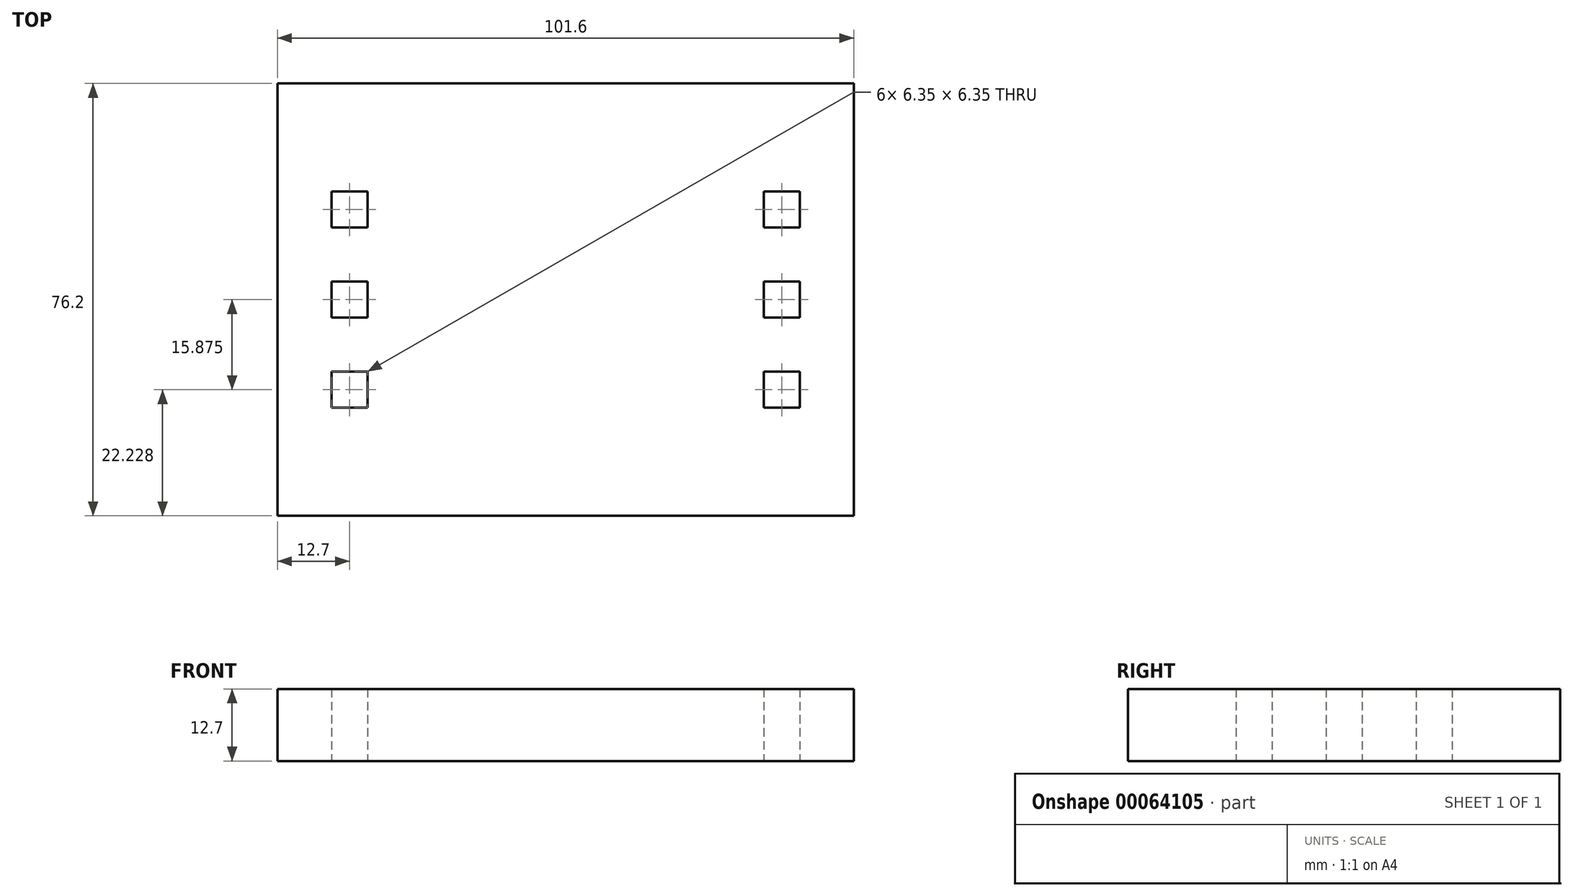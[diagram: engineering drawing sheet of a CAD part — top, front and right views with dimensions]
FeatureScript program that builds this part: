
annotation { "Feature Type Name" : "Feature", "Feature Type Description" : "" }
export const myFeature = defineFeature(function(context is Context, id is Id, definition is map)
    precondition{}
    {
        {
            var Q0;
            Q0=qCreatedBy(makeId("Top.planeOp"),FACE);
            var sketch = newSketch(context, id + "F0", { "sketchPlane" : qUnion([Q0])});
            skLineSegment(sketch, "E0.bottom", {"start": v(-40.85, 46.24) * mm, "end": v(60.75, 46.24) * mm});
            skLineSegment(sketch, "E0.top", {"start": v(-40.85, -29.96) * mm, "end": v(60.75, -29.96) * mm});
            skLineSegment(sketch, "E0.left", {"start": v(-40.85, 46.24) * mm, "end": v(-40.85, -29.96) * mm});
            skLineSegment(sketch, "E0.right", {"start": v(60.75, 46.24) * mm, "end": v(60.75, -29.96) * mm});
            skLineSegment(sketch, "E1.0", {"start": v(-40.85, 39.9) * mm, "end": v(60.75, 39.9) * mm, "construction": true});
            skLineSegment(sketch, "E2.0", {"start": v(-40.85, -23.6) * mm, "end": v(60.75, -23.6) * mm, "construction": true});
            skLineSegment(sketch, "E3.0", {"start": v(48.05, 46.24) * mm, "end": v(48.05, -29.96) * mm});
            skLineSegment(sketch, "E4.0", {"start": v(-28.15, 46.24) * mm, "end": v(-28.15, -29.96) * mm, "construction": true});
            skLineSegment(sketch, "E5", {"start": v(-40.85, 8.14) * mm, "end": v(60.75, 8.14) * mm, "construction": true});
            skLineSegment(sketch, "E6", {"start": v(9.95, 46.24) * mm, "end": v(9.95, -29.96) * mm, "construction": true});
            skLineSegment(sketch, "E7", {"start": v(48.05, 39.9) * mm, "end": v(48.05, 8.14) * mm, "construction": true});
            skLineSegment(sketch, "E8.0", {"start": v(41.7, 39.9) * mm, "end": v(41.7, 8.14) * mm, "construction": true});
            skLineSegment(sketch, "E9.0", {"start": v(54.4, 39.9) * mm, "end": v(54.4, 8.14) * mm, "construction": true});
            skLineSegment(sketch, "E10.0", {"start": v(41.7, 46.24) * mm, "end": v(41.7, -29.96) * mm});
            skLineSegment(sketch, "E11.0", {"start": v(54.4, 46.24) * mm, "end": v(54.4, -29.96) * mm, "construction": true});
            skLineSegment(sketch, "E12", {"start": v(48.05, 24.02) * mm, "end": v(54.4, 24.02) * mm, "construction": true});
            skLineSegment(sketch, "E13", {"start": v(48.05, 24.02) * mm, "end": v(41.7, 24.02) * mm, "construction": true});
            skLineSegment(sketch, "E14", {"start": v(48.05, 8.14) * mm, "end": v(54.4, 8.14) * mm, "construction": true});
            skLineSegment(sketch, "E15", {"start": v(41.7, 8.14) * mm, "end": v(48.05, 8.14) * mm, "construction": true});
            skLineSegment(sketch, "E16", {"start": v(44.88, 8.14) * mm, "end": v(44.88, 11.32) * mm});
            skLineSegment(sketch, "E17", {"start": v(44.88, 11.32) * mm, "end": v(51.23, 11.32) * mm});
            skPoint(sketch, "E17.endSnap0", {"position": v(51.23, 8.14) * mm});
            skLineSegment(sketch, "E18", {"start": v(51.23, 11.32) * mm, "end": v(51.23, 8.14) * mm});
            skLineSegment(sketch, "E19", {"start": v(44.88, 24.02) * mm, "end": v(44.88, 27.2) * mm});
            skLineSegment(sketch, "E20", {"start": v(44.88, 27.2) * mm, "end": v(51.23, 27.2) * mm});
            skPoint(sketch, "E20.endSnap0", {"position": v(51.23, 24.02) * mm});
            skLineSegment(sketch, "E21", {"start": v(51.23, 27.2) * mm, "end": v(51.23, 24.02) * mm});
            skLineSegment(sketch, "E22.MirrorCS", {"start": v(44.88, -7.73) * mm, "end": v(44.88, -10.9) * mm});
            skLineSegment(sketch, "E23.MirrorCS", {"start": v(44.88, -10.9) * mm, "end": v(51.23, -10.9) * mm});
            skPoint(sketch, "E24.MirrorP", {"position": v(51.23, -7.73) * mm});
            skLineSegment(sketch, "E25.MirrorCS", {"start": v(51.23, 20.84) * mm, "end": v(51.23, 24.02) * mm});
            skLineSegment(sketch, "E26.MirrorCS", {"start": v(44.88, 20.84) * mm, "end": v(51.23, 20.84) * mm});
            skLineSegment(sketch, "E27.MirrorCS", {"start": v(44.88, 24.02) * mm, "end": v(44.88, 20.84) * mm});
            skLineSegment(sketch, "E28.MirrorCS", {"start": v(44.88, 8.14) * mm, "end": v(44.88, 4.97) * mm});
            skLineSegment(sketch, "E29.MirrorCS", {"start": v(44.88, 4.97) * mm, "end": v(51.23, 4.97) * mm});
            skLineSegment(sketch, "E30.MirrorCS", {"start": v(51.23, 4.97) * mm, "end": v(51.23, 8.14) * mm});
            skLineSegment(sketch, "E31.MirrorCS", {"start": v(51.23, -10.9) * mm, "end": v(51.23, -7.73) * mm});
            skLineSegment(sketch, "E32.MirrorCS", {"start": v(51.23, -4.56) * mm, "end": v(51.23, -7.73) * mm});
            skLineSegment(sketch, "E33.MirrorCS", {"start": v(44.88, -4.56) * mm, "end": v(51.23, -4.56) * mm});
            skLineSegment(sketch, "E34.MirrorCS", {"start": v(44.88, -7.73) * mm, "end": v(44.88, -4.56) * mm});
            skLineSegment(sketch, "E35.MirrorCS", {"start": v(-24.97, 27.2) * mm, "end": v(-31.32, 27.2) * mm});
            skLineSegment(sketch, "E36.MirrorCS", {"start": v(-31.32, 27.2) * mm, "end": v(-31.32, 24.02) * mm});
            skLineSegment(sketch, "E37.MirrorCS", {"start": v(-31.32, 20.84) * mm, "end": v(-31.32, 24.02) * mm});
            skLineSegment(sketch, "E38.MirrorCS", {"start": v(-24.97, 20.84) * mm, "end": v(-31.32, 20.84) * mm});
            skLineSegment(sketch, "E39.MirrorCS", {"start": v(-24.97, 24.02) * mm, "end": v(-24.97, 20.84) * mm});
            skLineSegment(sketch, "E40.MirrorCS", {"start": v(-24.97, 24.02) * mm, "end": v(-24.97, 27.2) * mm});
            skLineSegment(sketch, "E41.MirrorCS", {"start": v(-24.97, 11.32) * mm, "end": v(-31.32, 11.32) * mm});
            skLineSegment(sketch, "E42.MirrorCS", {"start": v(-24.97, 8.14) * mm, "end": v(-24.97, 11.32) * mm});
            skLineSegment(sketch, "E43.MirrorCS", {"start": v(-24.97, 8.14) * mm, "end": v(-24.97, 4.97) * mm});
            skLineSegment(sketch, "E44.MirrorCS", {"start": v(-24.97, 4.97) * mm, "end": v(-31.32, 4.97) * mm});
            skLineSegment(sketch, "E45.MirrorCS", {"start": v(-31.32, 4.97) * mm, "end": v(-31.32, 8.14) * mm});
            skLineSegment(sketch, "E46.MirrorCS", {"start": v(-31.32, 11.32) * mm, "end": v(-31.32, 8.14) * mm});
            skLineSegment(sketch, "E47.MirrorCS", {"start": v(-24.97, -4.56) * mm, "end": v(-31.32, -4.56) * mm});
            skLineSegment(sketch, "E48.MirrorCS", {"start": v(-31.32, -4.56) * mm, "end": v(-31.32, -7.73) * mm});
            skLineSegment(sketch, "E49.MirrorCS", {"start": v(-31.32, -10.9) * mm, "end": v(-31.32, -7.73) * mm});
            skLineSegment(sketch, "E50.MirrorCS", {"start": v(-24.97, -10.9) * mm, "end": v(-31.32, -10.9) * mm});
            skLineSegment(sketch, "E51.MirrorCS", {"start": v(-24.97, -7.73) * mm, "end": v(-24.97, -10.9) * mm});
            skLineSegment(sketch, "E52.MirrorCS", {"start": v(-24.97, -7.73) * mm, "end": v(-24.97, -4.56) * mm});
            skLineSegment(sketch, "E53.MirrorCS", {"start": v(-34.5, 39.9) * mm, "end": v(-34.5, 8.14) * mm, "construction": true});
            skLineSegment(sketch, "E54.MirrorCS", {"start": v(-21.8, 46.24) * mm, "end": v(-21.8, -29.96) * mm});
            skLineSegment(sketch, "E55.MirrorCS", {"start": v(-34.5, 46.24) * mm, "end": v(-34.5, -29.96) * mm, "construction": true});
            skLineSegment(sketch, "E56", {"start": v(-21.8, 8.14) * mm, "end": v(41.7, 8.14) * mm, "construction": true});
            skLineSegment(sketch, "E57", {"start": v(-21.8, 28.92) * mm, "end": v(41.7, 28.92) * mm, "construction": true});
            skSolve(sketch);
        }
        {
            var Q0;
            Q0 = qSketchRegion(id + "F0", true);
            extrude(context, id + "F1", {"entities" : qUnion([Q0]), "depth" : 12.7 * mm});
        }
    });
